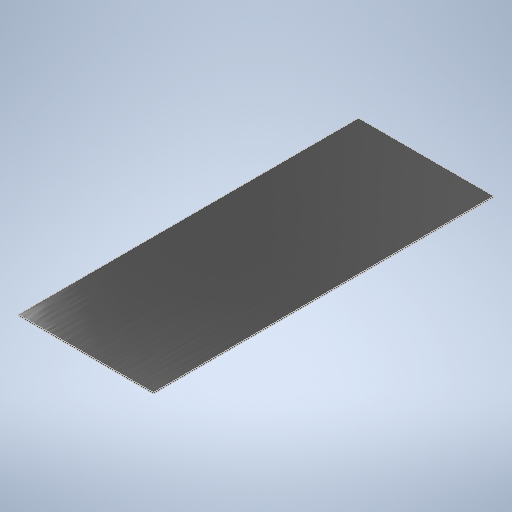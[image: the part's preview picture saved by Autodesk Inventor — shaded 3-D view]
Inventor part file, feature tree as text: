
AUTODESK INVENTOR PART (.ipt)
format: ipt  version: 2025.1 (Build 291241020, 241B)  size: 240,640 bytes
history: native  units: in
note: dims shown in document units (in); Inventor stores cm internally (conversion verified against a paired STEP export)
features: extrude x1, sketch x1
ambient origin geometry x8: Origin, YZ Plane, XZ Plane, XY Plane, X Axis, Y Axis, Z Axis, Center Point
bodies: Solid1 (feature_tree)
feature tree (2):
  extrude  "Extrusion1"  Depth=33.375in
  sketch  "Sketch1"  dims[d0=13.25in d1=33.375in d2=0.125in d3=0.0in]
